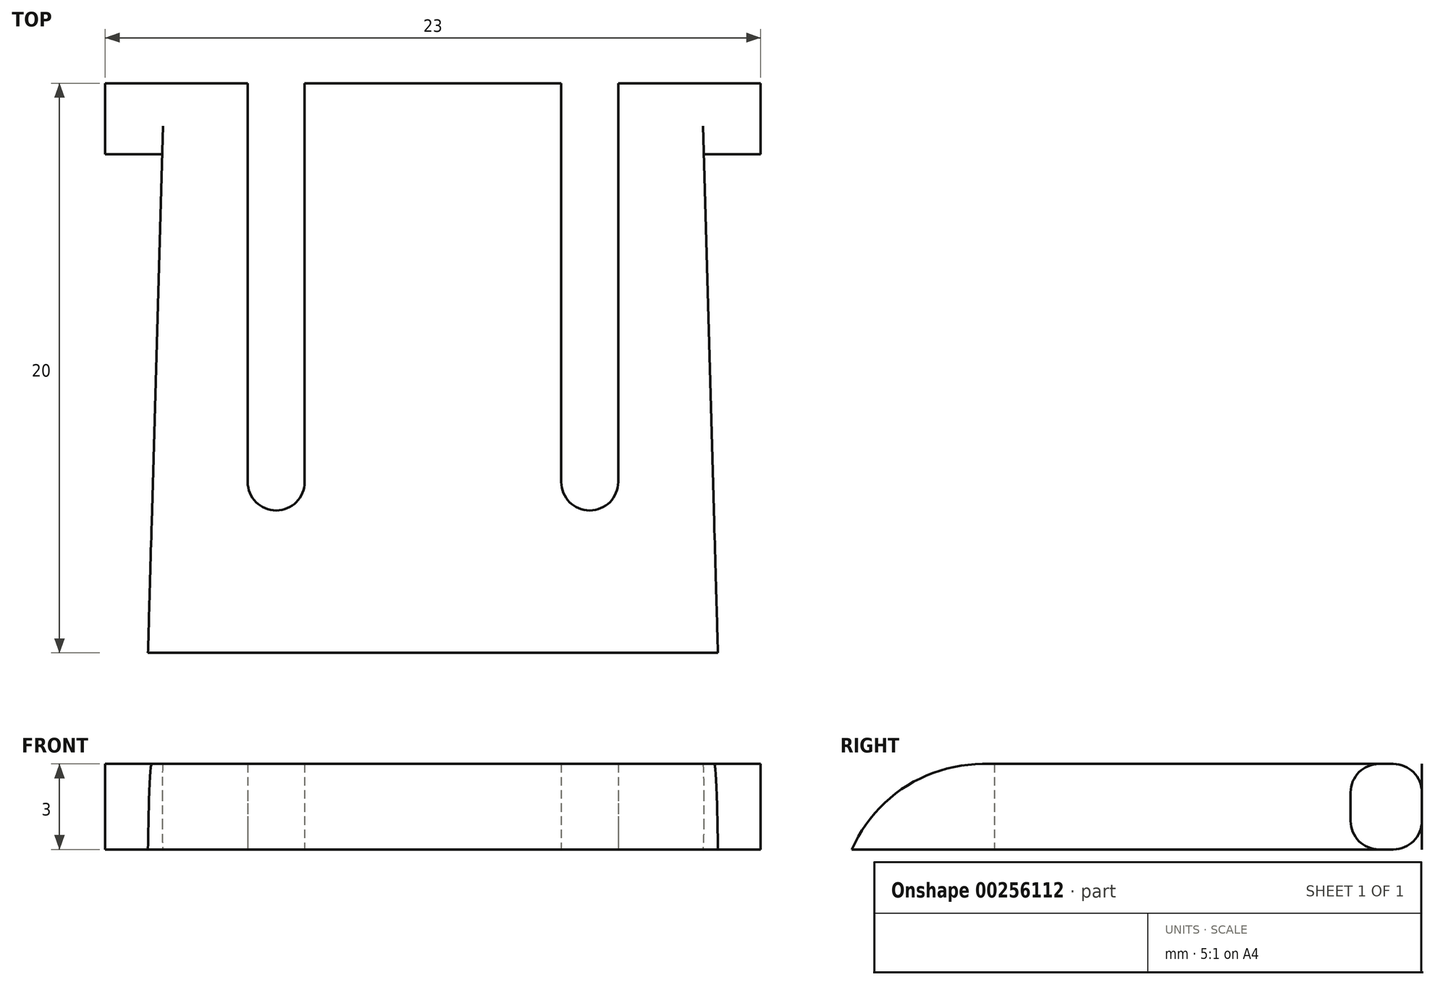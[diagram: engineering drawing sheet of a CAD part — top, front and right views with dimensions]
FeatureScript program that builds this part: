
annotation { "Feature Type Name" : "Feature", "Feature Type Description" : "" }
export const myFeature = defineFeature(function(context is Context, id is Id, definition is map)
    precondition{}
    {
        {
            var Q0;
            Q0=qCreatedBy(makeId("Top.planeOp"),FACE);
            var sketch = newSketch(context, id + "F0", { "sketchPlane" : qUnion([Q0])});
            skLineSegment(sketch, "E0", {"start": v(0, 0) * mm, "end": v(10, 0) * mm});
            skLineSegment(sketch, "E1", {"start": v(0, 20) * mm, "end": v(4.5, 20) * mm});
            skLineSegment(sketch, "E2", {"start": v(4.5, 20) * mm, "end": v(4.5, 6) * mm});
            skLineSegment(sketch, "E3", {"start": v(6.5, 6) * mm, "end": v(6.5, 20) * mm});
            skLineSegment(sketch, "E4", {"start": v(6.5, 20) * mm, "end": v(11.5, 20) * mm});
            skLineSegment(sketch, "E5", {"start": v(11.5, 20) * mm, "end": v(11.5, 17.5) * mm});
            skLineSegment(sketch, "E6", {"start": v(11.5, 17.5) * mm, "end": v(9.5, 17.5) * mm});
            skLineSegment(sketch, "E7", {"start": v(9.5, 17.5) * mm, "end": v(10, 0) * mm});
            skArc(sketch, "E8", {"start": v(4.5, 6) * mm, "mid": v(5.5, 5) * mm, "end": v(6.5, 6) * mm});
            skLineSegment(sketch, "E9", {"start": v(0, 20) * mm, "end": v(0, 0) * mm});
            skSolve(sketch);
        }
        {
            var Q0;
            Q0=makeQuery(id+"F0.imprint","IMPRINT",FACE,{"disambiguationData":[TD([[makeQuery(id+"F0.imprint","IMPRINT",EDGE,{"derivedFrom":sQuery(id+"F0.wireOp",EDGE,"E0")}),1.0]])]});
            extrude(context, id + "F4", {"entities" : qUnion([Q0]), "depth" : 3 * mm});
        }
        {
            var Q0;
            Q0=makeQuery(id+"F4.opExtrude","CAP_EDGE",EDGE,{"disambiguationData":[OSD([sQuery(id+"F0.wireOp",EDGE,"E6")])],"isStart":false});
            var Q1;
            Q1=makeQuery(id+"F4.opExtrude","CAP_EDGE",EDGE,{"disambiguationData":[OSD([sQuery(id+"F0.wireOp",EDGE,"E4")])],"isStart":false});
            var Q2;
            Q2=makeQuery(id+"F4.opExtrude","CAP_EDGE",EDGE,{"disambiguationData":[OSD([sQuery(id+"F0.wireOp",EDGE,"E6")])],"isStart":true});
            var Q3;
            Q3=makeQuery(id+"F4.opExtrude","CAP_EDGE",EDGE,{"disambiguationData":[OSD([sQuery(id+"F0.wireOp",EDGE,"E4")])],"isStart":true});
            fillet(context, id + "F1", {"entities" : qUnion([Q0, Q1, Q2, Q3]), "radius" : 1 * mm, "tangentPropagation" : true, "allowEdgeOverflow" : false});
        }
        {
            var Q0;
            Q0=makeQuery(id+"F4.opExtrude","SWEPT_BODY",BODY,{"disambiguationData":[OSD([sQuery(id+"F0.wireOp",EDGE,"E0"),sQuery(id+"F0.wireOp",EDGE,"E1"),sQuery(id+"F0.wireOp",EDGE,"E2"),sQuery(id+"F0.wireOp",EDGE,"E3"),sQuery(id+"F0.wireOp",EDGE,"E4"),sQuery(id+"F0.wireOp",EDGE,"E5"),sQuery(id+"F0.wireOp",EDGE,"E6"),sQuery(id+"F0.wireOp",EDGE,"E7"),sQuery(id+"F0.wireOp",EDGE,"E8"),sQuery(id+"F0.wireOp",EDGE,"E9")])]});
            var Q1;
            Q1=qCreatedBy(makeId("Right.planeOp"),FACE);
            mirror(context, id + "F2", {"operationType" : NewBodyOperationType.ADD, "entities" : qUnion([Q0]), "mirrorPlane" : qUnion([Q1])});
        }
        {
            var Q0;
            {var subQ0=makeQuery(id+"F4.opExtrude","CAP_EDGE",EDGE,{"disambiguationData":[OSD([sQuery(id+"F0.wireOp",EDGE,"E0")])],"isStart":false});Q0=makeQuery(id+"F2.boolean.opBoolean","MERGE",EDGE,{"derivedFrom":[subQ0,makeQuery(id+"F2.opPattern","COPY",EDGE,{"derivedFrom":subQ0,"instanceName":"1"})]});}
            fillet(context, id + "F3", {"entities" : qUnion([Q0]), "radius" : 5 * mm, "tangentPropagation" : true, "allowEdgeOverflow" : false});
        }
    });
